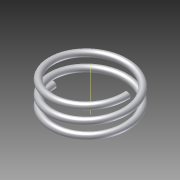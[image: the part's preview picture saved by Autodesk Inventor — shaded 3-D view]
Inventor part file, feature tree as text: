
AUTODESK INVENTOR PART (.ipt)
format: ipt  version: 2012 (Build 160160000, 160)  size: 272,896 bytes
history: native  units: in
note: dims shown in document units (in); Inventor stores cm internally (conversion verified against a paired STEP export)
features: helix x1, sketch x1
ambient origin geometry x8: Origin, YZ Plane, XZ Plane, XY Plane, X Axis, Y Axis, Z Axis, Center Point
feature tree (2):
  helix  "Coil2"  [1 undecoded]
  sketch  "Sketch2"  dims[d11=0.6625in d12=0.25in d13=0.5in d14=0.7874in d15=0.0in d16=90.0deg d17=90.0deg d18=0.0in d19=0.0in]
note: 1 required parameter value undecoded (feature->parameter linkage not recoverable at this tier; creation-order binding heuristic only, values carry confidence <= 0.55)
